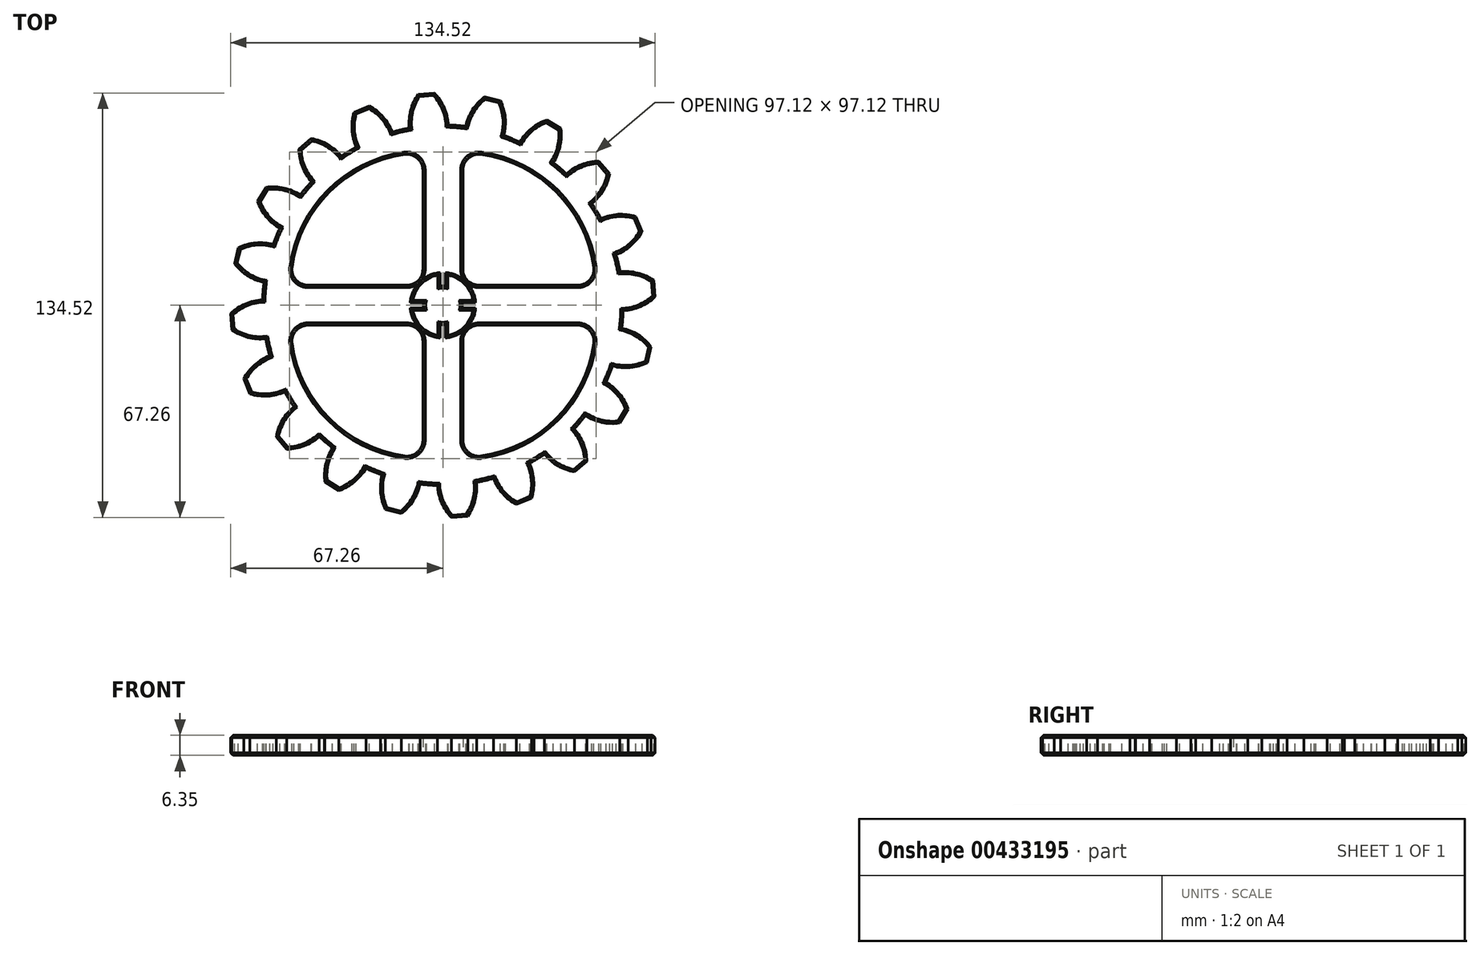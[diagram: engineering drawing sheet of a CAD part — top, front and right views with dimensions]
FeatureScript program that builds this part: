
annotation { "Feature Type Name" : "Feature", "Feature Type Description" : "" }
export const myFeature = defineFeature(function(context is Context, id is Id, definition is map)
    precondition{}
    {
        {
            var Q0;
            Q0=qCreatedBy(makeId("Top.planeOp"),FACE);
            var sketch = newSketch(context, id + "F0", { "sketchPlane" : qUnion([Q0])});
            skCircle(sketch, "E0", {"center": v(0, 0) * mm, "radius": 30.48 * mm, "construction": true});
            skSolve(sketch);
        }
        {
            var Q0;
            Q0=qCreatedBy(makeId("Top.planeOp"),FACE);
            var sketch = newSketch(context, id + "F1", { "sketchPlane" : qUnion([Q0])});
            skCircle(sketch, "E1", {"center": v(0, 0) * mm, "radius": 67.31 * mm, "construction": true});
            skCircle(sketch, "E2", {"center": v(0, 0) * mm, "radius": 63.5 * mm, "construction": true});
            skCircle(sketch, "E3", {"center": v(0, 0) * mm, "radius": 57.15 * mm, "construction": true});
            skLineSegment(sketch, "E4", {"start": v(0, 0) * mm, "end": v(0, 89.78) * mm, "construction": true});
            skLineSegment(sketch, "E5", {"start": v(0, 0) * mm, "end": v(-7.61, 96.72) * mm, "construction": true});
            skLineSegment(sketch, "E6", {"start": v(0, 63.5) * mm, "end": v(-65.71, 63.5) * mm, "construction": true});
            skLineSegment(sketch, "E7", {"start": v(0, 63.5) * mm, "end": v(-58.85, 37.3) * mm, "construction": true});
            skCircle(sketch, "E8", {"center": v(0, 63.5) * mm, "radius": 15.88 * mm, "construction": true});
            skCircle(sketch, "E9", {"center": v(0, 0) * mm, "radius": 58.01 * mm, "construction": true});
            skCircle(sketch, "E10", {"center": v(-14.13, 56.26) * mm, "radius": 15.88 * mm, "construction": true});
            skArc(sketch, "E11", {"start": v(1.72, 57.12) * mm, "mid": v(0.43, 62.59) * mm, "end": v(-2.68, 67.26) * mm});
            skArc(sketch, "E12.MirrorCS", {"start": v(-10.64, 56.15) * mm, "mid": v(-10.22, 61.75) * mm, "end": v(-7.88, 66.85) * mm});
            skLineSegment(sketch, "E13", {"start": v(-7.88, 66.85) * mm, "end": v(-2.68, 67.26) * mm});
            skArc(sketch, "E14", {"start": v(-10.64, 56.15) * mm, "mid": v(4.48, -56.97) * mm, "end": v(1.72, 57.12) * mm});
            skSolve(sketch);
        }
        {
            var Q0;
            Q0=qSketchRegion(id+"F1",true);
            var Q1;
            Q1=makeQuery(id+"Ffi0VH93psu6soF_0.opExtrude","CAP_FACE",FACE,{"disambiguationData":[OSD([sQuery(id+"F0.wireOp",EDGE,"E0")])],"isStart":true});
            extrude(context, id + "F2", {"entities" : qUnion([Q0]), "oppositeDirection" : true, "endBoundEntityFace" : qUnion([Q1]), "depth" : 6.35 * mm});
        }
        {
            var Q0;
            Q0=makeQuery(id+"F2.opExtrude","SWEPT_BODY",BODY,{"disambiguationData":[OSD([sQuery(id+"F1.wireOp",EDGE,"E11"),sQuery(id+"F1.wireOp",EDGE,"E12.MirrorCS"),sQuery(id+"F1.wireOp",EDGE,"E13"),sQuery(id+"F1.wireOp",EDGE,"ZPE7Z8ba-rLlS-d3gG-Tl0h-fifcE816pJjn")])]});
            var Q1;
            Q1=sQuery(id+"F0.wireOp",EDGE,"E0");
            circularPattern(context, id + "F3", {"operationType" : NewBodyOperationType.ADD, "entities" : qUnion([Q0]), "axis" : qUnion([Q1]), "angle" : 360 * degree, "instanceCount" : 20, "equalSpace" : true});
        }
        {
            var Q0;
            {var subQ0=makeQuery(id+"F2.opExtrude","CAP_FACE",FACE,{"disambiguationData":[OSD([sQuery(id+"F1.wireOp",EDGE,"E11"),sQuery(id+"F1.wireOp",EDGE,"E12.MirrorCS"),sQuery(id+"F1.wireOp",EDGE,"E13"),sQuery(id+"F1.wireOp",EDGE,"ZPE7Z8ba-rLlS-d3gG-Tl0h-fifcE816pJjn")])],"isStart":true});Q0=makeQuery(id+"F3.boolean.opBoolean","MERGE",FACE,{"derivedFrom":[makeQuery(id+"Ffi0VH93psu6soF_0.opExtrude","CAP_FACE",FACE,{"disambiguationData":[OSD([sQuery(id+"F0.wireOp",EDGE,"E0")])],"isStart":false}),subQ0,makeQuery(id+"F3.opPattern","COPY",FACE,{"derivedFrom":subQ0,"instanceName":"1"}),makeQuery(id+"F3.opPattern","COPY",FACE,{"derivedFrom":subQ0,"instanceName":"2"}),makeQuery(id+"F3.opPattern","COPY",FACE,{"derivedFrom":subQ0,"instanceName":"3"}),makeQuery(id+"F3.opPattern","COPY",FACE,{"derivedFrom":subQ0,"instanceName":"4"}),makeQuery(id+"F3.opPattern","COPY",FACE,{"derivedFrom":subQ0,"instanceName":"5"}),makeQuery(id+"F3.opPattern","COPY",FACE,{"derivedFrom":subQ0,"instanceName":"6"}),makeQuery(id+"F3.opPattern","COPY",FACE,{"derivedFrom":subQ0,"instanceName":"7"}),makeQuery(id+"F3.opPattern","COPY",FACE,{"derivedFrom":subQ0,"instanceName":"8"}),makeQuery(id+"F3.opPattern","COPY",FACE,{"derivedFrom":subQ0,"instanceName":"9"}),makeQuery(id+"F3.opPattern","COPY",FACE,{"derivedFrom":subQ0,"instanceName":"10"}),makeQuery(id+"F3.opPattern","COPY",FACE,{"derivedFrom":subQ0,"instanceName":"11"}),makeQuery(id+"F3.opPattern","COPY",FACE,{"derivedFrom":subQ0,"instanceName":"12"}),makeQuery(id+"F3.opPattern","COPY",FACE,{"derivedFrom":subQ0,"instanceName":"13"}),makeQuery(id+"F3.opPattern","COPY",FACE,{"derivedFrom":subQ0,"instanceName":"14"})]});}
            var sketch = newSketch(context, id + "F4", { "sketchPlane" : qUnion([Q0])});
            skLineSegment(sketch, "E15", {"start": v(-6.35, 6.35) * mm, "end": v(-48.17, 6.35) * mm});
            skLineSegment(sketch, "E16", {"start": v(-6.35, 6.35) * mm, "end": v(-6.35, 48.17) * mm});
            skArc(sketch, "E17", {"start": v(-6.35, 48.17) * mm, "mid": v(-35.92, 35.92) * mm, "end": v(-48.17, 6.35) * mm});
            skArc(sketch, "E18.1.0", {"start": v(-48.17, -6.35) * mm, "mid": v(-35.92, -35.92) * mm, "end": v(-6.35, -48.17) * mm});
            skLineSegment(sketch, "E18.1.1", {"start": v(-6.35, -6.35) * mm, "end": v(-48.17, -6.35) * mm});
            skLineSegment(sketch, "E18.1.2", {"start": v(-6.35, -6.35) * mm, "end": v(-6.35, -48.17) * mm});
            skArc(sketch, "E18.2.0", {"start": v(6.35, -48.17) * mm, "mid": v(35.92, -35.92) * mm, "end": v(48.17, -6.35) * mm});
            skLineSegment(sketch, "E18.2.1", {"start": v(6.35, -6.35) * mm, "end": v(6.35, -48.17) * mm});
            skLineSegment(sketch, "E18.2.2", {"start": v(6.35, -6.35) * mm, "end": v(48.17, -6.35) * mm});
            skArc(sketch, "E18.3.0", {"start": v(48.17, 6.35) * mm, "mid": v(35.92, 35.92) * mm, "end": v(6.35, 48.17) * mm});
            skLineSegment(sketch, "E18.3.1", {"start": v(6.35, 6.35) * mm, "end": v(48.17, 6.35) * mm});
            skLineSegment(sketch, "E18.3.2", {"start": v(6.35, 6.35) * mm, "end": v(6.35, 48.17) * mm});
            skPoint(sketch, "E18.center", {"position": v(0, 0) * mm});
            skSolve(sketch);
        }
        {
            var Q0;
            Q0=qSketchRegion(id+"F4",true);
            extrude(context, id + "F5", {"entities" : qUnion([Q0]), "operationType" : NewBodyOperationType.REMOVE, "endBound" : BoundingType.THROUGH_ALL, "oppositeDirection" : true, "depth" : 25.4 * mm});
        }
        {
            var Q0;
            Q0=makeQuery(id+"F5.boolean.opBoolean","COPY",EDGE,{"derivedFrom":makeQuery(id+"F5.opExtrude","SWEPT_EDGE",EDGE,{"disambiguationData":[OSD([sQuery(id+"F4.wireOp",EDGE,"E18.1.0"),sQuery(id+"F4.wireOp",EDGE,"E18.1.1")])]})});
            var Q1;
            Q1=makeQuery(id+"F5.boolean.opBoolean","COPY",EDGE,{"derivedFrom":makeQuery(id+"F5.opExtrude","SWEPT_EDGE",EDGE,{"disambiguationData":[OSD([sQuery(id+"F4.wireOp",EDGE,"E18.1.1"),sQuery(id+"F4.wireOp",EDGE,"E18.1.2")])]})});
            var Q2;
            Q2=makeQuery(id+"F5.boolean.opBoolean","COPY",EDGE,{"derivedFrom":makeQuery(id+"F5.opExtrude","SWEPT_EDGE",EDGE,{"disambiguationData":[OSD([sQuery(id+"F4.wireOp",EDGE,"E18.1.0"),sQuery(id+"F4.wireOp",EDGE,"E18.1.2")])]})});
            var Q3;
            Q3=makeQuery(id+"F5.boolean.opBoolean","COPY",EDGE,{"derivedFrom":makeQuery(id+"F5.opExtrude","SWEPT_EDGE",EDGE,{"disambiguationData":[OSD([sQuery(id+"F4.wireOp",EDGE,"E18.2.1"),sQuery(id+"F4.wireOp",EDGE,"E18.2.2")])]})});
            var Q4;
            Q4=makeQuery(id+"F5.boolean.opBoolean","COPY",EDGE,{"derivedFrom":makeQuery(id+"F5.opExtrude","SWEPT_EDGE",EDGE,{"disambiguationData":[OSD([sQuery(id+"F4.wireOp",EDGE,"E18.2.0"),sQuery(id+"F4.wireOp",EDGE,"E18.2.2")])]})});
            var Q5;
            Q5=makeQuery(id+"F5.boolean.opBoolean","COPY",EDGE,{"derivedFrom":makeQuery(id+"F5.opExtrude","SWEPT_EDGE",EDGE,{"disambiguationData":[OSD([sQuery(id+"F4.wireOp",EDGE,"E18.3.1"),sQuery(id+"F4.wireOp",EDGE,"E18.3.2")])]})});
            var Q6;
            Q6=makeQuery(id+"F5.boolean.opBoolean","COPY",EDGE,{"derivedFrom":makeQuery(id+"F5.opExtrude","SWEPT_EDGE",EDGE,{"disambiguationData":[OSD([sQuery(id+"F4.wireOp",EDGE,"E18.3.0"),sQuery(id+"F4.wireOp",EDGE,"E18.3.2")])]})});
            var Q7;
            Q7=makeQuery(id+"F5.boolean.opBoolean","COPY",EDGE,{"derivedFrom":makeQuery(id+"F5.opExtrude","SWEPT_EDGE",EDGE,{"disambiguationData":[OSD([sQuery(id+"F4.wireOp",EDGE,"E18.3.0"),sQuery(id+"F4.wireOp",EDGE,"E18.3.1")])]})});
            var Q8;
            Q8=makeQuery(id+"F5.boolean.opBoolean","COPY",EDGE,{"derivedFrom":makeQuery(id+"F5.opExtrude","SWEPT_EDGE",EDGE,{"disambiguationData":[OSD([sQuery(id+"F4.wireOp",EDGE,"E15"),sQuery(id+"F4.wireOp",EDGE,"E17")])]})});
            var Q9;
            Q9=makeQuery(id+"F5.boolean.opBoolean","COPY",EDGE,{"derivedFrom":makeQuery(id+"F5.opExtrude","SWEPT_EDGE",EDGE,{"disambiguationData":[OSD([sQuery(id+"F4.wireOp",EDGE,"E15"),sQuery(id+"F4.wireOp",EDGE,"E16")])]})});
            var Q10;
            Q10=makeQuery(id+"F5.boolean.opBoolean","COPY",EDGE,{"derivedFrom":makeQuery(id+"F5.opExtrude","SWEPT_EDGE",EDGE,{"disambiguationData":[OSD([sQuery(id+"F4.wireOp",EDGE,"E16"),sQuery(id+"F4.wireOp",EDGE,"E17")])]})});
            var Q11;
            Q11=makeQuery(id+"F5.boolean.opBoolean","COPY",EDGE,{"derivedFrom":makeQuery(id+"F5.opExtrude","SWEPT_EDGE",EDGE,{"disambiguationData":[OSD([sQuery(id+"F4.wireOp",EDGE,"E18.2.0"),sQuery(id+"F4.wireOp",EDGE,"E18.2.1")])]})});
            fillet(context, id + "F6", {"entities" : qUnion([Q0, Q1, Q2, Q3, Q4, Q5, Q6, Q7, Q8, Q9, Q10, Q11]), "radius" : 5.08 * mm, "tangentPropagation" : true, "allowEdgeOverflow" : false});
        }
        {
            var Q0;
            {var subQ0=makeQuery(id+"F2.opExtrude","CAP_FACE",FACE,{"disambiguationData":[OSD([sQuery(id+"F1.wireOp",EDGE,"E11"),sQuery(id+"F1.wireOp",EDGE,"E12.MirrorCS"),sQuery(id+"F1.wireOp",EDGE,"E13"),sQuery(id+"F1.wireOp",EDGE,"E14")])],"isStart":true});Q0=makeQuery(id+"F3.boolean.opBoolean","MERGE",FACE,{"derivedFrom":[subQ0,makeQuery(id+"F3.opPattern","COPY",FACE,{"derivedFrom":subQ0,"instanceName":"1"}),makeQuery(id+"F3.opPattern","COPY",FACE,{"derivedFrom":subQ0,"instanceName":"2"}),makeQuery(id+"F3.opPattern","COPY",FACE,{"derivedFrom":subQ0,"instanceName":"3"}),makeQuery(id+"F3.opPattern","COPY",FACE,{"derivedFrom":subQ0,"instanceName":"4"}),makeQuery(id+"F3.opPattern","COPY",FACE,{"derivedFrom":subQ0,"instanceName":"5"}),makeQuery(id+"F3.opPattern","COPY",FACE,{"derivedFrom":subQ0,"instanceName":"6"}),makeQuery(id+"F3.opPattern","COPY",FACE,{"derivedFrom":subQ0,"instanceName":"7"}),makeQuery(id+"F3.opPattern","COPY",FACE,{"derivedFrom":subQ0,"instanceName":"8"}),makeQuery(id+"F3.opPattern","COPY",FACE,{"derivedFrom":subQ0,"instanceName":"9"}),makeQuery(id+"F3.opPattern","COPY",FACE,{"derivedFrom":subQ0,"instanceName":"10"}),makeQuery(id+"F3.opPattern","COPY",FACE,{"derivedFrom":subQ0,"instanceName":"11"}),makeQuery(id+"F3.opPattern","COPY",FACE,{"derivedFrom":subQ0,"instanceName":"12"}),makeQuery(id+"F3.opPattern","COPY",FACE,{"derivedFrom":subQ0,"instanceName":"13"}),makeQuery(id+"F3.opPattern","COPY",FACE,{"derivedFrom":subQ0,"instanceName":"14"}),makeQuery(id+"F3.opPattern","COPY",FACE,{"derivedFrom":subQ0,"instanceName":"15"}),makeQuery(id+"F3.opPattern","COPY",FACE,{"derivedFrom":subQ0,"instanceName":"16"}),makeQuery(id+"F3.opPattern","COPY",FACE,{"derivedFrom":subQ0,"instanceName":"17"}),makeQuery(id+"F3.opPattern","COPY",FACE,{"derivedFrom":subQ0,"instanceName":"18"}),makeQuery(id+"F3.opPattern","COPY",FACE,{"derivedFrom":subQ0,"instanceName":"19"}),makeQuery(id+"F3.opPattern","COPY",FACE,{"derivedFrom":subQ0,"instanceName":"20"}),makeQuery(id+"F3.opPattern","COPY",FACE,{"derivedFrom":subQ0,"instanceName":"21"}),makeQuery(id+"F3.opPattern","COPY",FACE,{"derivedFrom":subQ0,"instanceName":"22"}),makeQuery(id+"F3.opPattern","COPY",FACE,{"derivedFrom":subQ0,"instanceName":"23"})]});}
            var sketch = newSketch(context, id + "F7", { "sketchPlane" : qUnion([Q0])});
            skCircle(sketch, "E19", {"center": v(0, 0) * mm, "radius": 9.65 * mm});
            skSolve(sketch);
        }
        {
            var Q0;
            Q0=qSketchRegion(id+"F7",true);
            extrude(context, id + "F8", {"entities" : qUnion([Q0]), "operationType" : NewBodyOperationType.REMOVE, "oppositeDirection" : true, "depth" : 19.05 * mm});
        }
        {
            var Q0;
            {var subQ0=makeQuery(id+"F2.opExtrude","CAP_FACE",FACE,{"disambiguationData":[OSD([sQuery(id+"F1.wireOp",EDGE,"E11"),sQuery(id+"F1.wireOp",EDGE,"E12.MirrorCS"),sQuery(id+"F1.wireOp",EDGE,"E13"),sQuery(id+"F1.wireOp",EDGE,"E14")])],"isStart":true});Q0=makeQuery(id+"F3.boolean.opBoolean","MERGE",FACE,{"derivedFrom":[subQ0,makeQuery(id+"F3.opPattern","COPY",FACE,{"derivedFrom":subQ0,"instanceName":"1"}),makeQuery(id+"F3.opPattern","COPY",FACE,{"derivedFrom":subQ0,"instanceName":"2"}),makeQuery(id+"F3.opPattern","COPY",FACE,{"derivedFrom":subQ0,"instanceName":"3"}),makeQuery(id+"F3.opPattern","COPY",FACE,{"derivedFrom":subQ0,"instanceName":"4"}),makeQuery(id+"F3.opPattern","COPY",FACE,{"derivedFrom":subQ0,"instanceName":"5"}),makeQuery(id+"F3.opPattern","COPY",FACE,{"derivedFrom":subQ0,"instanceName":"6"}),makeQuery(id+"F3.opPattern","COPY",FACE,{"derivedFrom":subQ0,"instanceName":"7"}),makeQuery(id+"F3.opPattern","COPY",FACE,{"derivedFrom":subQ0,"instanceName":"8"}),makeQuery(id+"F3.opPattern","COPY",FACE,{"derivedFrom":subQ0,"instanceName":"9"}),makeQuery(id+"F3.opPattern","COPY",FACE,{"derivedFrom":subQ0,"instanceName":"10"}),makeQuery(id+"F3.opPattern","COPY",FACE,{"derivedFrom":subQ0,"instanceName":"11"}),makeQuery(id+"F3.opPattern","COPY",FACE,{"derivedFrom":subQ0,"instanceName":"12"}),makeQuery(id+"F3.opPattern","COPY",FACE,{"derivedFrom":subQ0,"instanceName":"13"}),makeQuery(id+"F3.opPattern","COPY",FACE,{"derivedFrom":subQ0,"instanceName":"14"}),makeQuery(id+"F3.opPattern","COPY",FACE,{"derivedFrom":subQ0,"instanceName":"15"}),makeQuery(id+"F3.opPattern","COPY",FACE,{"derivedFrom":subQ0,"instanceName":"16"}),makeQuery(id+"F3.opPattern","COPY",FACE,{"derivedFrom":subQ0,"instanceName":"17"}),makeQuery(id+"F3.opPattern","COPY",FACE,{"derivedFrom":subQ0,"instanceName":"18"}),makeQuery(id+"F3.opPattern","COPY",FACE,{"derivedFrom":subQ0,"instanceName":"19"})]});}
            var sketch = newSketch(context, id + "F9", { "sketchPlane" : qUnion([Q0])});
            skArc(sketch, "E20", {"start": v(1.59, 5.16) * mm, "mid": v(0, 5.4) * mm, "end": v(-1.59, 5.16) * mm});
            skLineSegment(sketch, "E21.bottom", {"start": v(-1.59, 9.65) * mm, "end": v(1.59, 9.65) * mm});
            skLineSegment(sketch, "E21.left", {"start": v(-1.59, 9.65) * mm, "end": v(-1.59, 5.16) * mm});
            skLineSegment(sketch, "E21.right", {"start": v(1.59, 9.65) * mm, "end": v(1.59, 5.16) * mm});
            skLineSegment(sketch, "E22.1.0", {"start": v(-9.65, -1.59) * mm, "end": v(-9.65, 1.59) * mm});
            skLineSegment(sketch, "E22.1.1", {"start": v(-9.65, 1.59) * mm, "end": v(-5.16, 1.59) * mm});
            skLineSegment(sketch, "E22.1.2", {"start": v(-9.65, -1.59) * mm, "end": v(-5.16, -1.59) * mm});
            skArc(sketch, "E22.1.3", {"start": v(-5.16, 1.59) * mm, "mid": v(-5.4, 0) * mm, "end": v(-5.16, -1.59) * mm});
            skLineSegment(sketch, "E22.2.0", {"start": v(1.59, -9.65) * mm, "end": v(-1.59, -9.65) * mm});
            skLineSegment(sketch, "E22.2.1", {"start": v(-1.59, -9.65) * mm, "end": v(-1.59, -5.16) * mm});
            skLineSegment(sketch, "E22.2.2", {"start": v(1.59, -9.65) * mm, "end": v(1.59, -5.16) * mm});
            skArc(sketch, "E22.2.3", {"start": v(-1.59, -5.16) * mm, "mid": v(0, -5.4) * mm, "end": v(1.59, -5.16) * mm});
            skLineSegment(sketch, "E22.3.0", {"start": v(9.65, 1.59) * mm, "end": v(9.65, -1.59) * mm});
            skLineSegment(sketch, "E22.3.1", {"start": v(9.65, -1.59) * mm, "end": v(5.16, -1.59) * mm});
            skLineSegment(sketch, "E22.3.2", {"start": v(9.65, 1.59) * mm, "end": v(5.16, 1.59) * mm});
            skArc(sketch, "E22.3.3", {"start": v(5.16, -1.59) * mm, "mid": v(5.4, 0) * mm, "end": v(5.16, 1.59) * mm});
            skSolve(sketch);
        }
        {
            var Q0;
            Q0 = qSketchRegion(id + "F9", true);
            var Q1;
            {var subQ0=makeQuery(id+"F2.opExtrude","CAP_FACE",FACE,{"disambiguationData":[OSD([sQuery(id+"F1.wireOp",EDGE,"E11"),sQuery(id+"F1.wireOp",EDGE,"E12.MirrorCS"),sQuery(id+"F1.wireOp",EDGE,"E13"),sQuery(id+"F1.wireOp",EDGE,"E14")])],"isStart":false});Q1=makeQuery(id+"F3.boolean.opBoolean","MERGE",FACE,{"derivedFrom":[subQ0,makeQuery(id+"F3.opPattern","COPY",FACE,{"derivedFrom":subQ0,"instanceName":"1"}),makeQuery(id+"F3.opPattern","COPY",FACE,{"derivedFrom":subQ0,"instanceName":"2"}),makeQuery(id+"F3.opPattern","COPY",FACE,{"derivedFrom":subQ0,"instanceName":"3"}),makeQuery(id+"F3.opPattern","COPY",FACE,{"derivedFrom":subQ0,"instanceName":"4"}),makeQuery(id+"F3.opPattern","COPY",FACE,{"derivedFrom":subQ0,"instanceName":"5"}),makeQuery(id+"F3.opPattern","COPY",FACE,{"derivedFrom":subQ0,"instanceName":"6"}),makeQuery(id+"F3.opPattern","COPY",FACE,{"derivedFrom":subQ0,"instanceName":"7"}),makeQuery(id+"F3.opPattern","COPY",FACE,{"derivedFrom":subQ0,"instanceName":"8"}),makeQuery(id+"F3.opPattern","COPY",FACE,{"derivedFrom":subQ0,"instanceName":"9"}),makeQuery(id+"F3.opPattern","COPY",FACE,{"derivedFrom":subQ0,"instanceName":"10"}),makeQuery(id+"F3.opPattern","COPY",FACE,{"derivedFrom":subQ0,"instanceName":"11"}),makeQuery(id+"F3.opPattern","COPY",FACE,{"derivedFrom":subQ0,"instanceName":"12"}),makeQuery(id+"F3.opPattern","COPY",FACE,{"derivedFrom":subQ0,"instanceName":"13"}),makeQuery(id+"F3.opPattern","COPY",FACE,{"derivedFrom":subQ0,"instanceName":"14"}),makeQuery(id+"F3.opPattern","COPY",FACE,{"derivedFrom":subQ0,"instanceName":"15"}),makeQuery(id+"F3.opPattern","COPY",FACE,{"derivedFrom":subQ0,"instanceName":"16"}),makeQuery(id+"F3.opPattern","COPY",FACE,{"derivedFrom":subQ0,"instanceName":"17"}),makeQuery(id+"F3.opPattern","COPY",FACE,{"derivedFrom":subQ0,"instanceName":"18"}),makeQuery(id+"F3.opPattern","COPY",FACE,{"derivedFrom":subQ0,"instanceName":"19"})]});}
            extrude(context, id + "F10", {"entities" : qUnion([Q0]), "operationType" : NewBodyOperationType.ADD, "endBound" : BoundingType.UP_TO_SURFACE, "oppositeDirection" : true, "depth" : 25.4 * mm, "endBoundEntityFace" : qUnion([Q1]), "offsetDistance" : 25.4 * mm});
        }
        {
            var Q0;
            {var subQ0=makeQuery(id+"F2.opExtrude","CAP_FACE",FACE,{"disambiguationData":[OSD([sQuery(id+"F1.wireOp",EDGE,"E11"),sQuery(id+"F1.wireOp",EDGE,"E12.MirrorCS"),sQuery(id+"F1.wireOp",EDGE,"E13"),sQuery(id+"F1.wireOp",EDGE,"E14")])],"isStart":false});Q0=makeQuery(id+"F3.boolean.opBoolean","MERGE",FACE,{"derivedFrom":[subQ0,makeQuery(id+"F3.opPattern","COPY",FACE,{"derivedFrom":subQ0,"instanceName":"1"}),makeQuery(id+"F3.opPattern","COPY",FACE,{"derivedFrom":subQ0,"instanceName":"2"}),makeQuery(id+"F3.opPattern","COPY",FACE,{"derivedFrom":subQ0,"instanceName":"3"}),makeQuery(id+"F3.opPattern","COPY",FACE,{"derivedFrom":subQ0,"instanceName":"4"}),makeQuery(id+"F3.opPattern","COPY",FACE,{"derivedFrom":subQ0,"instanceName":"5"}),makeQuery(id+"F3.opPattern","COPY",FACE,{"derivedFrom":subQ0,"instanceName":"6"}),makeQuery(id+"F3.opPattern","COPY",FACE,{"derivedFrom":subQ0,"instanceName":"7"}),makeQuery(id+"F3.opPattern","COPY",FACE,{"derivedFrom":subQ0,"instanceName":"8"}),makeQuery(id+"F3.opPattern","COPY",FACE,{"derivedFrom":subQ0,"instanceName":"9"}),makeQuery(id+"F3.opPattern","COPY",FACE,{"derivedFrom":subQ0,"instanceName":"10"}),makeQuery(id+"F3.opPattern","COPY",FACE,{"derivedFrom":subQ0,"instanceName":"11"}),makeQuery(id+"F3.opPattern","COPY",FACE,{"derivedFrom":subQ0,"instanceName":"12"}),makeQuery(id+"F3.opPattern","COPY",FACE,{"derivedFrom":subQ0,"instanceName":"13"}),makeQuery(id+"F3.opPattern","COPY",FACE,{"derivedFrom":subQ0,"instanceName":"14"}),makeQuery(id+"F3.opPattern","COPY",FACE,{"derivedFrom":subQ0,"instanceName":"15"}),makeQuery(id+"F3.opPattern","COPY",FACE,{"derivedFrom":subQ0,"instanceName":"16"}),makeQuery(id+"F3.opPattern","COPY",FACE,{"derivedFrom":subQ0,"instanceName":"17"}),makeQuery(id+"F3.opPattern","COPY",FACE,{"derivedFrom":subQ0,"instanceName":"18"}),makeQuery(id+"F3.opPattern","COPY",FACE,{"derivedFrom":subQ0,"instanceName":"19"})]});}
            var Q1;
            {var subQ0=makeQuery(id+"F2.opExtrude","CAP_FACE",FACE,{"disambiguationData":[OSD([sQuery(id+"F1.wireOp",EDGE,"E11"),sQuery(id+"F1.wireOp",EDGE,"E12.MirrorCS"),sQuery(id+"F1.wireOp",EDGE,"E13"),sQuery(id+"F1.wireOp",EDGE,"E14")])],"isStart":true});Q1=makeQuery(id+"F3.boolean.opBoolean","MERGE",FACE,{"derivedFrom":[subQ0,makeQuery(id+"F3.opPattern","COPY",FACE,{"derivedFrom":subQ0,"instanceName":"1"}),makeQuery(id+"F3.opPattern","COPY",FACE,{"derivedFrom":subQ0,"instanceName":"2"}),makeQuery(id+"F3.opPattern","COPY",FACE,{"derivedFrom":subQ0,"instanceName":"3"}),makeQuery(id+"F3.opPattern","COPY",FACE,{"derivedFrom":subQ0,"instanceName":"4"}),makeQuery(id+"F3.opPattern","COPY",FACE,{"derivedFrom":subQ0,"instanceName":"5"}),makeQuery(id+"F3.opPattern","COPY",FACE,{"derivedFrom":subQ0,"instanceName":"6"}),makeQuery(id+"F3.opPattern","COPY",FACE,{"derivedFrom":subQ0,"instanceName":"7"}),makeQuery(id+"F3.opPattern","COPY",FACE,{"derivedFrom":subQ0,"instanceName":"8"}),makeQuery(id+"F3.opPattern","COPY",FACE,{"derivedFrom":subQ0,"instanceName":"9"}),makeQuery(id+"F3.opPattern","COPY",FACE,{"derivedFrom":subQ0,"instanceName":"10"}),makeQuery(id+"F3.opPattern","COPY",FACE,{"derivedFrom":subQ0,"instanceName":"11"}),makeQuery(id+"F3.opPattern","COPY",FACE,{"derivedFrom":subQ0,"instanceName":"12"}),makeQuery(id+"F3.opPattern","COPY",FACE,{"derivedFrom":subQ0,"instanceName":"13"}),makeQuery(id+"F3.opPattern","COPY",FACE,{"derivedFrom":subQ0,"instanceName":"14"}),makeQuery(id+"F3.opPattern","COPY",FACE,{"derivedFrom":subQ0,"instanceName":"15"}),makeQuery(id+"F3.opPattern","COPY",FACE,{"derivedFrom":subQ0,"instanceName":"16"}),makeQuery(id+"F3.opPattern","COPY",FACE,{"derivedFrom":subQ0,"instanceName":"17"}),makeQuery(id+"F3.opPattern","COPY",FACE,{"derivedFrom":subQ0,"instanceName":"18"}),makeQuery(id+"F3.opPattern","COPY",FACE,{"derivedFrom":subQ0,"instanceName":"19"})]});}
            chamfer(context, id + "F11", {"entities" : qUnion([Q0, Q1]), "width" : 0.76 * mm, "tangentPropagation" : true});
        }
    });
